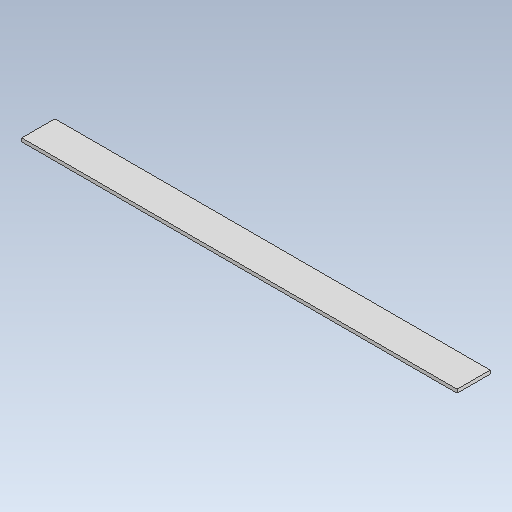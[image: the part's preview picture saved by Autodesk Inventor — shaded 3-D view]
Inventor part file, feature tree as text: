
AUTODESK INVENTOR PART (.ipt)
format: ipt  version: 2020.1 (Build 241239000, 239)  size: 95,232 bytes
history: native  units: mm
features: other x1, extrude x1, sketch x1
ambient origin geometry x8: Origin, YZ Plane, XZ Plane, XY Plane, X Axis, Y Axis, Z Axis, Center Point
bodies: Body1 (feature_tree)
feature tree (3):
  other  "Твердое тело1"
  extrude  "Выдавливание1"  Depth=1000.0mm
  sketch  "Эскиз1"
